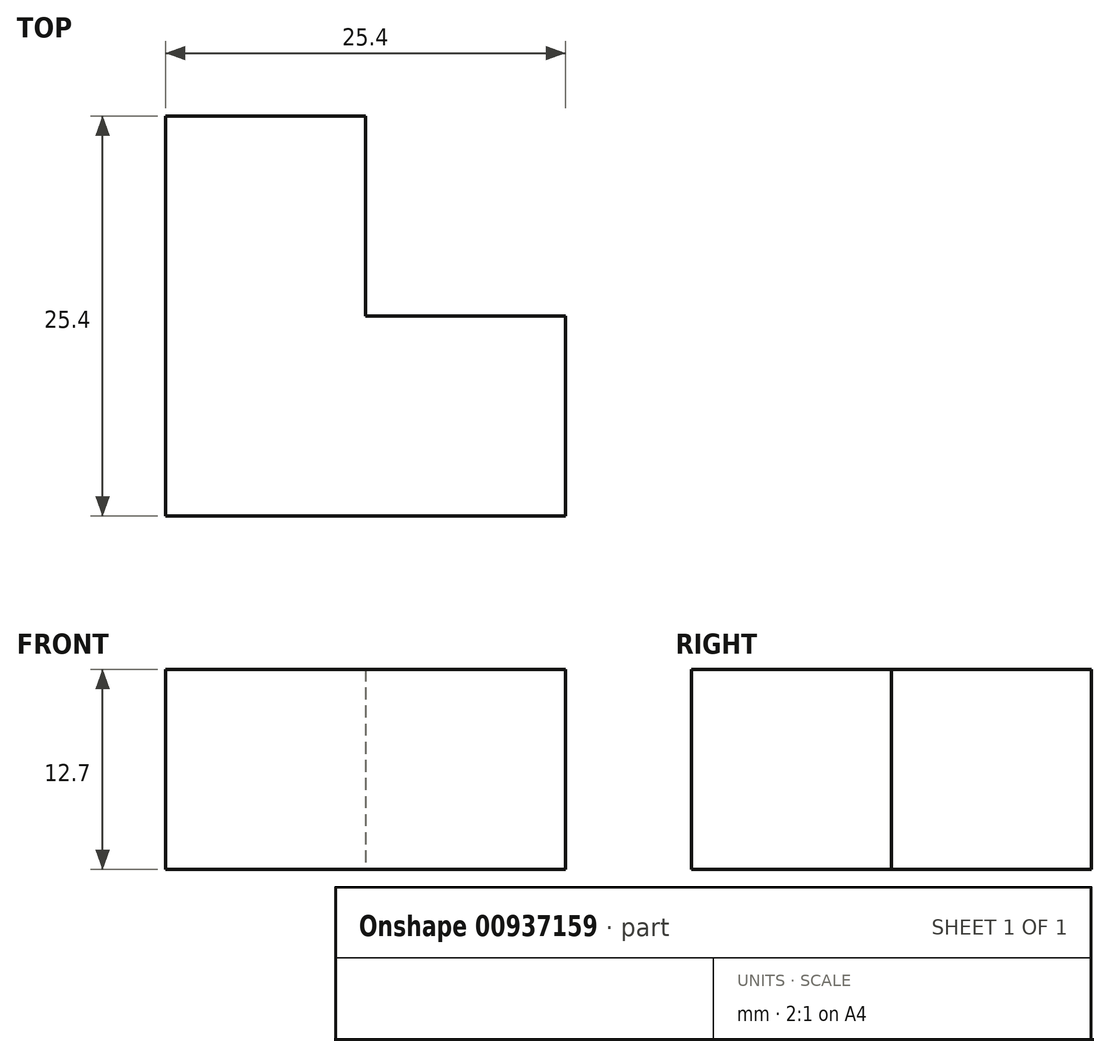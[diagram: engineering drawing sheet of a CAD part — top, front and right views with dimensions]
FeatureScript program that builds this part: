
annotation { "Feature Type Name" : "Feature", "Feature Type Description" : "" }
export const myFeature = defineFeature(function(context is Context, id is Id, definition is map)
    precondition{}
    {
        {
            var Q0;
            Q0=qCreatedBy(makeId("Front.planeOp"),FACE);
            var sketch = newSketch(context, id + "F0", { "sketchPlane" : qUnion([Q0])});
            skLineSegment(sketch, "E0.bottom", {"start": v(-54.01, 26.07) * mm, "end": v(-41.31, 26.07) * mm});
            skLineSegment(sketch, "E0.top", {"start": v(-54.01, 13.37) * mm, "end": v(-41.31, 13.37) * mm});
            skLineSegment(sketch, "E0.left", {"start": v(-54.01, 26.07) * mm, "end": v(-54.01, 13.37) * mm});
            skLineSegment(sketch, "E0.right", {"start": v(-41.31, 26.07) * mm, "end": v(-41.31, 13.37) * mm});
            skLineSegment(sketch, "E1.bottom", {"start": v(-41.31, 26.07) * mm, "end": v(-28.61, 26.07) * mm});
            skLineSegment(sketch, "E1.top", {"start": v(-41.31, 13.37) * mm, "end": v(-28.61, 13.37) * mm});
            skLineSegment(sketch, "E1.right", {"start": v(-28.61, 26.07) * mm, "end": v(-28.61, 13.37) * mm});
            skLineSegment(sketch, "E2.top", {"start": v(-41.31, 38.77) * mm, "end": v(-28.61, 38.77) * mm});
            skLineSegment(sketch, "E2.left", {"start": v(-41.31, 26.07) * mm, "end": v(-41.31, 38.77) * mm});
            skLineSegment(sketch, "E2.right", {"start": v(-28.61, 26.07) * mm, "end": v(-28.61, 38.77) * mm});
            skLineSegment(sketch, "E3.top", {"start": v(-41.31, 51.47) * mm, "end": v(-28.61, 51.47) * mm});
            skLineSegment(sketch, "E3.left", {"start": v(-41.31, 38.77) * mm, "end": v(-41.31, 51.47) * mm});
            skLineSegment(sketch, "E3.right", {"start": v(-28.61, 38.77) * mm, "end": v(-28.61, 51.47) * mm});
            skSolve(sketch);
        }
        {
            var Q0;
            Q0=makeQuery(id+"F0.imprint","IMPRINT",FACE,{"disambiguationData":[TD([[makeQuery(id+"F0.imprint","IMPRINT",EDGE,{"derivedFrom":sQuery(id+"F0.wireOp",EDGE,"E1.top")}),1.0]])]});
            var Q1;
            Q1=makeQuery(id+"F0.imprint","IMPRINT",FACE,{"disambiguationData":[TD([[makeQuery(id+"F0.imprint","IMPRINT",EDGE,{"derivedFrom":sQuery(id+"F0.wireOp",EDGE,"E1.bottom")}),1.0]])]});
            extrude(context, id + "F1", {"entities" : qUnion([Q0, Q1]), "depth" : 12.7 * mm, "offsetDistance" : 25.4 * mm});
        }
        {
            var Q0;
            Q0=makeQuery(id+"F0.imprint","IMPRINT",FACE,{"disambiguationData":[TD([[makeQuery(id+"F0.imprint","IMPRINT",EDGE,{"derivedFrom":sQuery(id+"F0.wireOp",EDGE,"E0.bottom")}),-1.0]])]});
            var Q1;
            Q1=makeQuery(id+"F0.imprint","IMPRINT",FACE,{"disambiguationData":[TD([[makeQuery(id+"F0.imprint","IMPRINT",EDGE,{"derivedFrom":sQuery(id+"F0.wireOp",EDGE,"E2.top")}),1.0]])]});
            extrude(context, id + "F2", {"entities" : qUnion([Q0, Q1]), "operationType" : NewBodyOperationType.ADD, "endBound" : BoundingType.SYMMETRIC, "depth" : 25.4 * mm, "offsetDistance" : 25.4 * mm});
        }
    });
